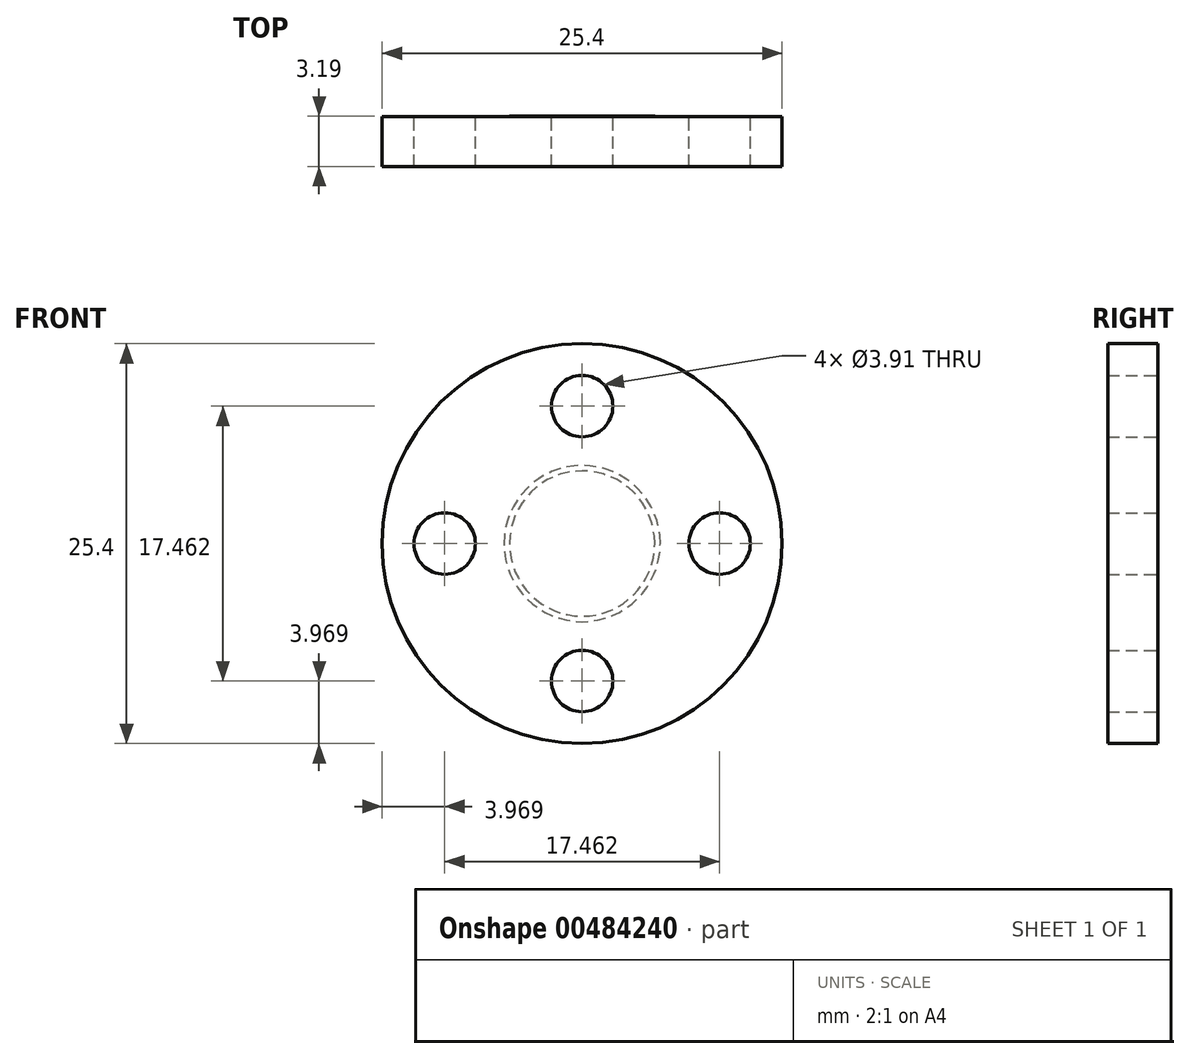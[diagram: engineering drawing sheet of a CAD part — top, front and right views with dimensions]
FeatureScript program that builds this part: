
annotation { "Feature Type Name" : "Feature", "Feature Type Description" : "" }
export const myFeature = defineFeature(function(context is Context, id is Id, definition is map)
    precondition{}
    {
        {
            var Q0;
            Q0=qCreatedBy(makeId("Front.planeOp"),FACE);
            var sketch = newSketch(context, id + "F0", { "sketchPlane" : qUnion([Q0])});
            skCircle(sketch, "E0", {"center": v(0, 0) * mm, "radius": 4.61 * mm});
            skSolve(sketch);
        }
        {
            var Q0;
            Q0 = qSketchRegion(id + "F0", true);
            extrude(context, id + "F1", {"entities" : qUnion([Q0]), "depth" : 1 / 101.6 * mm});
        }
        {
            var Q0;
            Q0=makeQuery(id+"F1.opExtrude","CAP_FACE",FACE,{"disambiguationData":[OSD([sQuery(id+"F0.wireOp",EDGE,"E0")])],"isStart":false});
            var sketch = newSketch(context, id + "F2", { "sketchPlane" : qUnion([Q0])});
            skCircle(sketch, "E1", {"center": v(0, 0) * mm, "radius": 4.96 * mm});
            skSolve(sketch);
        }
        {
            var Q0;
            Q0 = qSketchRegion(id + "F2", true);
            extrude(context, id + "F3", {"entities" : qUnion([Q0]), "operationType" : NewBodyOperationType.ADD, "depth" : 1 / 101.6 * mm});
        }
        {
            var Q0;
            Q0=makeQuery(id+"F3.opExtrude","CAP_FACE",FACE,{"disambiguationData":[OSD([sQuery(id+"F2.wireOp",EDGE,"E1")])],"isStart":false});
            var sketch = newSketch(context, id + "F4", { "sketchPlane" : qUnion([Q0])});
            skCircle(sketch, "E2", {"center": v(0, 0) * mm, "radius": 12.7 * mm});
            skCircle(sketch, "E3", {"center": v(0, 8.73) * mm, "radius": 1.95 * mm});
            skCircle(sketch, "E4.1.0", {"center": v(-8.73, 0) * mm, "radius": 1.95 * mm});
            skCircle(sketch, "E4.2.0", {"center": v(0, -8.73) * mm, "radius": 1.95 * mm});
            skCircle(sketch, "E4.3.0", {"center": v(8.73, 0) * mm, "radius": 1.95 * mm});
            skSolve(sketch);
        }
        {
            var Q0;
            Q0 = qSketchRegion(id + "F4", true);
            extrude(context, id + "F5", {"entities" : qUnion([Q0]), "operationType" : NewBodyOperationType.ADD, "depth" : 3.17 * mm});
        }
    });
